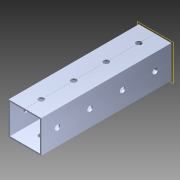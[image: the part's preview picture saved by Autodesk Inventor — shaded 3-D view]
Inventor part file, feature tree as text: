
AUTODESK INVENTOR PART (.ipt)
format: ipt  version: 2014 SP1 (Build 180222100, 222)  size: 1,131,008 bytes
history: native  units: in
note: dims shown in document units (in); Inventor stores cm internally (conversion verified against a paired STEP export)
features: pattern_circular x1, other x1, plane x1, extrude x1, imported_body x1, sketch x1
ambient origin geometry x8: Origin, YZ Plane, XZ Plane, XY Plane, X Axis, Y Axis, Z Axis, Center Point
bodies: Body1 (feature_tree)
feature tree (6):
  pattern_circular  "CirPattern2"
  other  "217-3426-STEP1"
  plane  "Work Plane1"
  extrude  "Extrusion1"  Depth=3937.0079in TaperAngle=0.0deg
  imported_body  "Base1"
  sketch  "Sketch1"  dims[d0=-4.0in d1=3937.0079in d2=0.0in]
